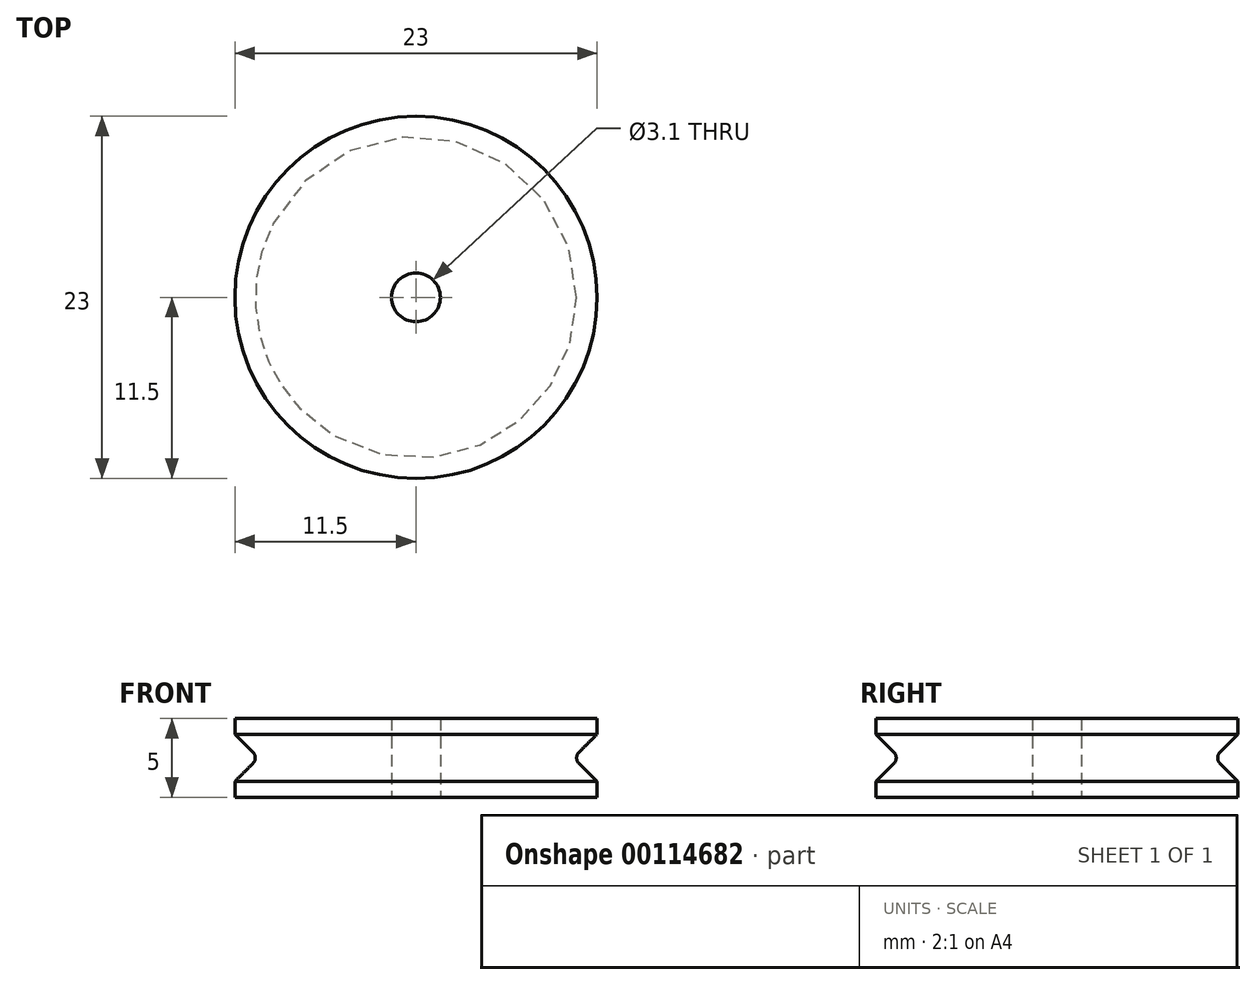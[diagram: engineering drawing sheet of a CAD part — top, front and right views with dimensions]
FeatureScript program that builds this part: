
annotation { "Feature Type Name" : "Feature", "Feature Type Description" : "" }
export const myFeature = defineFeature(function(context is Context, id is Id, definition is map)
    precondition{}
    {
        {
            var Q0;
            Q0=qCreatedBy(makeId("Top.planeOp"),FACE);
            var sketch = newSketch(context, id + "F0", { "sketchPlane" : qUnion([Q0])});
            skCircle(sketch, "E0", {"center": v(0, 0) * mm, "radius": 11.5 * mm});
            skLineSegment(sketch, "E1", {"start": v(-11.5, 0) * mm, "end": v(11.5, 0) * mm, "construction": true});
            skCircle(sketch, "E2", {"center": v(0, 0) * mm, "radius": 1.55 * mm});
            skSolve(sketch);
        }
        {
            var Q0;
            Q0=qCreatedBy(makeId("Front.planeOp"),FACE);
            var sketch = newSketch(context, id + "F1", { "sketchPlane" : qUnion([Q0])});
            skLineSegment(sketch, "E3", {"start": v(-11.5, 0) * mm, "end": v(-10, 1.5) * mm});
            skLineSegment(sketch, "E4", {"start": v(-10, 1.5) * mm, "end": v(-11.5, 3) * mm});
            skLineSegment(sketch, "E5", {"start": v(-11.5, 3) * mm, "end": v(-11.5, 0) * mm});
            skLineSegment(sketch, "E6", {"start": v(0, -9.23) * mm, "end": v(0, 13.09) * mm, "construction": true});
            skSolve(sketch);
        }
        {
            var Q0;
            Q0=makeQuery(id+"F0.imprint","IMPRINT",FACE,{"disambiguationData":[TD([[makeQuery(id+"F0.imprint","IMPRINT",EDGE,{"derivedFrom":sQuery(id+"F0.wireOp",EDGE,"E0")}),1.0]])]});
            extrude(context, id + "F2", {"entities" : qUnion([Q0]), "depth" : 4 * mm});
        }
        {
            var Q0;
            Q0=makeQuery(id+"F1.imprint","IMPRINT",FACE,{"disambiguationData":[TD([[makeQuery(id+"F1.imprint","IMPRINT",EDGE,{"derivedFrom":sQuery(id+"F1.wireOp",EDGE,"E3")}),1.0]])]});
            var Q1;
            Q1=sQuery(id+"F1.wireOp",EDGE,"E6");
            revolve(context, id + "F3", {"operationType" : NewBodyOperationType.REMOVE, "entities" : qUnion([Q0]), "axis" : qUnion([Q1]), "revolveType" : RevolveType.ONE_DIRECTION, "oppositeDirection" : true, "angle" : 360 * degree});
        }
        {
            var Q0;
            Q0=makeQuery(id+"F2.opExtrude","CAP_FACE",FACE,{"disambiguationData":[OSD([sQuery(id+"F0.wireOp",EDGE,"E0"),sQuery(id+"F0.wireOp",EDGE,"E2")])],"isStart":true});
            extrude(context, id + "F4", {"entities" : qUnion([Q0]), "operationType" : NewBodyOperationType.ADD, "depth" : 1 * mm});
        }
        {
            var Q0;
            Q0=makeQuery(id+"F3.boolean.opBoolean","COPY",EDGE,{"derivedFrom":makeQuery(id+"F3.opRevolve","SWEPT_EDGE",EDGE,{"disambiguationData":[OSD([sQuery(id+"F1.wireOp",EDGE,"E3"),sQuery(id+"F1.wireOp",EDGE,"E4")])]})});
            fillet(context, id + "F5", {"entities" : qUnion([Q0]), "radius" : 0.5 * mm, "tangentPropagation" : true, "allowEdgeOverflow" : false});
        }
    });
